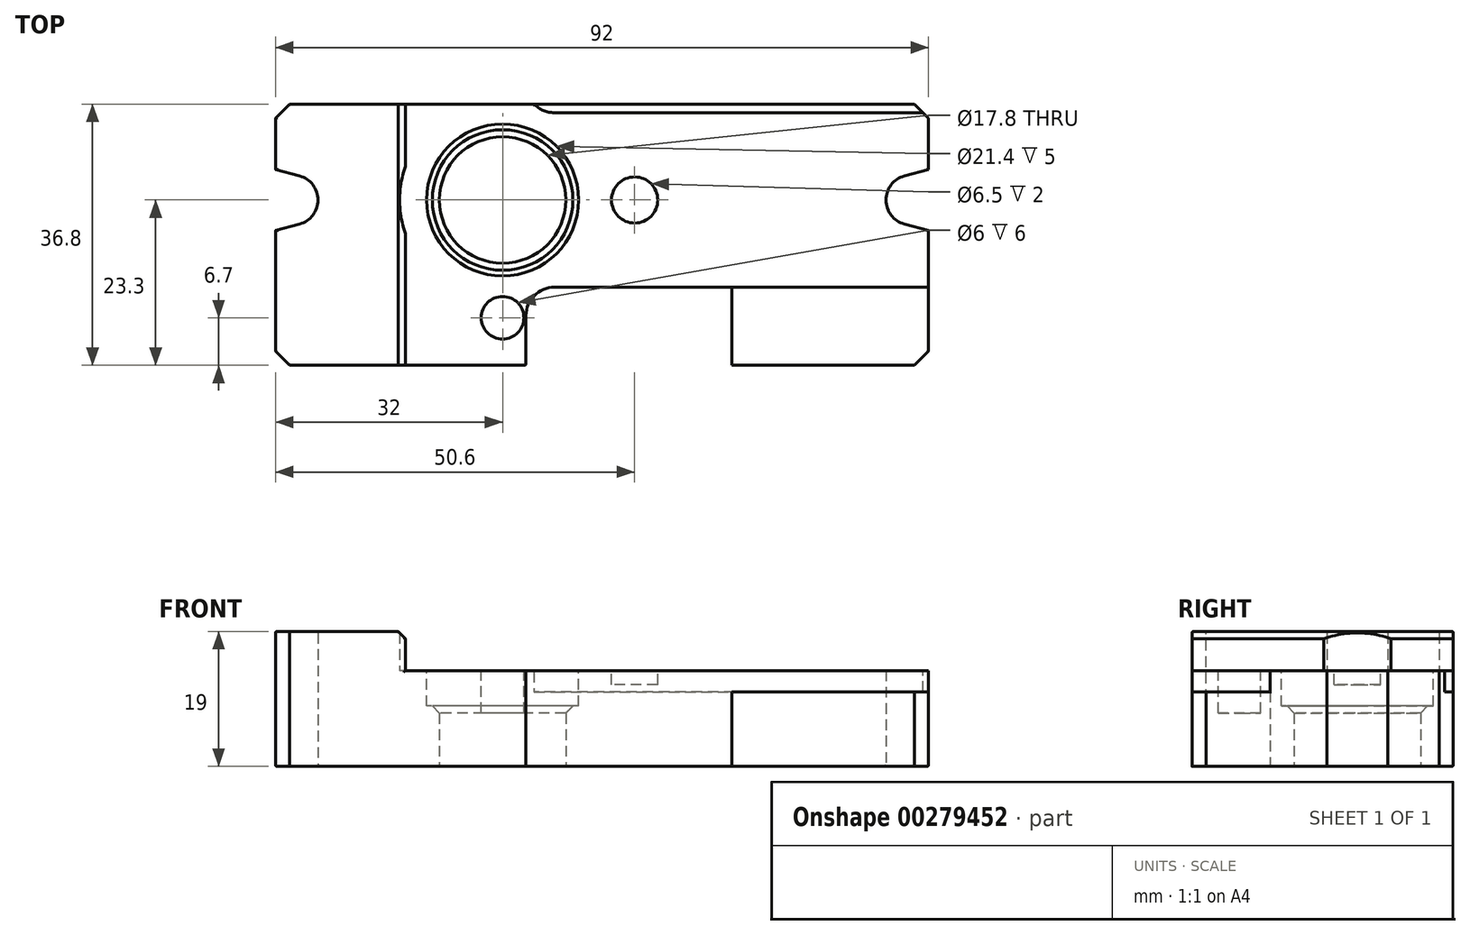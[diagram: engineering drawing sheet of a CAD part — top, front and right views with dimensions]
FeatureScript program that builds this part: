
annotation { "Feature Type Name" : "Feature", "Feature Type Description" : "" }
export const myFeature = defineFeature(function(context is Context, id is Id, definition is map)
    precondition{}
    {
        {
            var Q0;
            Q0=qCreatedBy(makeId("Top.planeOp"),FACE);
            var sketch = newSketch(context, id + "F0", { "sketchPlane" : qUnion([Q0])});
            skLineSegment(sketch, "E0", {"start": v(0, 0) * mm, "end": v(92, 0) * mm});
            skLineSegment(sketch, "E1", {"start": v(92, 0) * mm, "end": v(92, 19) * mm});
            skLineSegment(sketch, "E2", {"start": v(92, 36.8) * mm, "end": v(0, 36.8) * mm});
            skLineSegment(sketch, "E3", {"start": v(0, 36.8) * mm, "end": v(0, 27.6) * mm});
            skLineSegment(sketch, "E4", {"start": v(0, 0) * mm, "end": v(0, 23.3) * mm, "construction": true});
            skLineSegment(sketch, "E5", {"start": v(0, 23.3) * mm, "end": v(2.5, 23.3) * mm, "construction": true});
            skLineSegment(sketch, "E6", {"start": v(2.5, 23.3) * mm, "end": v(32, 23.3) * mm, "construction": true});
            skLineSegment(sketch, "E7", {"start": v(32, 23.3) * mm, "end": v(89.5, 23.3) * mm, "construction": true});
            skArc(sketch, "E8", {"start": v(3.4, 19.92) * mm, "mid": v(6, 23.3) * mm, "end": v(3.4, 26.68) * mm});
            skArc(sketch, "E9", {"start": v(88.6, 26.68) * mm, "mid": v(86, 23.3) * mm, "end": v(88.6, 19.92) * mm});
            skCircle(sketch, "E10", {"center": v(32, 23.3) * mm, "radius": 8.9 * mm});
            skCircle(sketch, "E11", {"center": v(32, 23.3) * mm, "radius": 10.7 * mm, "construction": true});
            skArc(sketch, "E12", {"start": v(18.3, 28.05) * mm, "mid": v(17.5, 23.3) * mm, "end": v(18.3, 18.55) * mm});
            skLineSegment(sketch, "E13", {"start": v(0, 36.8) * mm, "end": v(18.3, 36.8) * mm, "construction": true});
            skLineSegment(sketch, "E14", {"start": v(18.3, 36.8) * mm, "end": v(18.3, 28.05) * mm});
            skLineSegment(sketch, "E15.trimOffspring", {"start": v(18.3, 18.55) * mm, "end": v(18.3, 0) * mm});
            skLineSegment(sketch, "E16", {"start": v(3.4, 26.68) * mm, "end": v(0, 27.6) * mm});
            skLineSegment(sketch, "E17", {"start": v(3.4, 19.92) * mm, "end": v(0, 19) * mm});
            skLineSegment(sketch, "E18.trimOffspring", {"start": v(0, 19) * mm, "end": v(0, 0) * mm});
            skLineSegment(sketch, "E19", {"start": v(88.6, 26.68) * mm, "end": v(92, 27.6) * mm});
            skLineSegment(sketch, "E20", {"start": v(88.6, 19.92) * mm, "end": v(92, 19) * mm});
            skLineSegment(sketch, "E21.trimOffspring", {"start": v(92, 27.6) * mm, "end": v(92, 36.8) * mm});
            skLineSegment(sketch, "E22", {"start": v(0, 0) * mm, "end": v(50.6, 0) * mm, "construction": true});
            skLineSegment(sketch, "E23", {"start": v(50.6, 0) * mm, "end": v(50.6, 23.3) * mm, "construction": true});
            skCircle(sketch, "E24", {"center": v(50.6, 23.3) * mm, "radius": 3.25 * mm, "construction": true});
            skLineSegment(sketch, "E25", {"start": v(0, 0) * mm, "end": v(64.3, 0) * mm, "construction": true});
            skLineSegment(sketch, "E26", {"start": v(64.3, 0) * mm, "end": v(64.3, 36.8) * mm});
            skLineSegment(sketch, "E27", {"start": v(0, 36.8) * mm, "end": v(0, 39.6) * mm, "construction": true});
            skLineSegment(sketch, "E28", {"start": v(0, 39.6) * mm, "end": v(39.3, 39.6) * mm, "construction": true});
            skArc(sketch, "E29", {"start": v(36.44, 36.8) * mm, "mid": v(37.75, 35.91) * mm, "end": v(39.3, 35.6) * mm});
            skLineSegment(sketch, "E30", {"start": v(0, 36.8) * mm, "end": v(0, 35.6) * mm, "construction": true});
            skLineSegment(sketch, "E31", {"start": v(39.3, 35.6) * mm, "end": v(92, 35.6) * mm});
            skArc(sketch, "E32.MirrorC", {"start": v(35.3, 7) * mm, "mid": v(36.47, 9.83) * mm, "end": v(39.3, 11) * mm});
            skLineSegment(sketch, "E33.MirrorCS", {"start": v(39.3, 11) * mm, "end": v(92, 11) * mm});
            skLineSegment(sketch, "E34", {"start": v(35.3, 7) * mm, "end": v(35.3, 0) * mm});
            skLineSegment(sketch, "E35", {"start": v(32, 23.3) * mm, "end": v(32, 6.7) * mm, "construction": true});
            skCircle(sketch, "E36", {"center": v(32, 6.7) * mm, "radius": 3 * mm, "construction": true});
            skSolve(sketch);
        }
        {
            var Q0;
            Q0=qCreatedBy(makeId("Top.planeOp"),FACE);
            cPlane(context, id + "F1", {"entities" : qUnion([Q0]), "cplaneType" : CPlaneType.OFFSET, "offset" : 13.5 * mm, "width" : 150 * mm, "height" : 150 * mm});
        }
        {
            var Q0;
            Q0=qCreatedBy(id+"F1.planeOp",FACE);
            var sketch = newSketch(context, id + "F2", { "sketchPlane" : qUnion([Q0])});
            skCircle(sketch, "E37.0", {"center": v(32, 23.3) * mm, "radius": 10.7 * mm});
            skLineSegment(sketch, "E38.0.0", {"start": v(18.3, 0) * mm, "end": v(18.3, 18.55) * mm});
            skArc(sketch, "E38.0.1", {"start": v(18.3, 18.55) * mm, "mid": v(17.5, 23.3) * mm, "end": v(18.3, 28.05) * mm});
            skLineSegment(sketch, "E38.0.2", {"start": v(18.3, 28.05) * mm, "end": v(18.3, 36.8) * mm});
            skLineSegment(sketch, "E38.0.3", {"start": v(18.3, 36.8) * mm, "end": v(0, 36.8) * mm});
            skLineSegment(sketch, "E38.0.4", {"start": v(0, 36.8) * mm, "end": v(0, 27.6) * mm});
            skLineSegment(sketch, "E38.0.5", {"start": v(0, 27.6) * mm, "end": v(3.4, 26.68) * mm});
            skArc(sketch, "E38.0.6", {"start": v(3.4, 26.68) * mm, "mid": v(6, 23.3) * mm, "end": v(3.4, 19.92) * mm});
            skLineSegment(sketch, "E38.0.7", {"start": v(3.4, 19.92) * mm, "end": v(0, 19) * mm});
            skLineSegment(sketch, "E38.0.8", {"start": v(0, 19) * mm, "end": v(0, 0) * mm});
            skLineSegment(sketch, "E38.0.9", {"start": v(0, 0) * mm, "end": v(18.3, 0) * mm});
            skCircle(sketch, "E39.0", {"center": v(32, 6.7) * mm, "radius": 3 * mm});
            skCircle(sketch, "E40.0", {"center": v(50.6, 23.3) * mm, "radius": 3.25 * mm});
            skLineSegment(sketch, "E41.0.0", {"start": v(35.3, 0) * mm, "end": v(64.3, 0) * mm});
            skLineSegment(sketch, "E41.0.1", {"start": v(64.3, 0) * mm, "end": v(64.3, 11) * mm});
            skLineSegment(sketch, "E41.0.2", {"start": v(64.3, 11) * mm, "end": v(39.3, 11) * mm});
            skArc(sketch, "E41.0.3", {"start": v(39.3, 11) * mm, "mid": v(36.47, 9.83) * mm, "end": v(35.3, 7) * mm});
            skLineSegment(sketch, "E41.0.4", {"start": v(35.3, 7) * mm, "end": v(35.3, 0) * mm});
            skLineSegment(sketch, "E42.0.0", {"start": v(64.3, 11) * mm, "end": v(64.3, 0) * mm});
            skLineSegment(sketch, "E42.0.1", {"start": v(64.3, 0) * mm, "end": v(92, 0) * mm});
            skLineSegment(sketch, "E42.0.2", {"start": v(92, 0) * mm, "end": v(92, 11) * mm});
            skLineSegment(sketch, "E42.0.3", {"start": v(92, 11) * mm, "end": v(64.3, 11) * mm});
            skArc(sketch, "E43.0.0", {"start": v(36.44, 36.8) * mm, "mid": v(37.75, 35.91) * mm, "end": v(39.3, 35.6) * mm});
            skLineSegment(sketch, "E43.0.1", {"start": v(39.3, 35.6) * mm, "end": v(64.3, 35.6) * mm});
            skLineSegment(sketch, "E43.0.2", {"start": v(64.3, 35.6) * mm, "end": v(64.3, 36.8) * mm});
            skLineSegment(sketch, "E43.0.3", {"start": v(64.3, 36.8) * mm, "end": v(36.44, 36.8) * mm});
            skLineSegment(sketch, "E44.0.0", {"start": v(64.3, 36.8) * mm, "end": v(64.3, 35.6) * mm});
            skLineSegment(sketch, "E44.0.1", {"start": v(64.3, 35.6) * mm, "end": v(92, 35.6) * mm});
            skLineSegment(sketch, "E44.0.2", {"start": v(92, 35.6) * mm, "end": v(92, 36.8) * mm});
            skLineSegment(sketch, "E44.0.3", {"start": v(92, 36.8) * mm, "end": v(64.3, 36.8) * mm});
            skLineSegment(sketch, "E45.0.0", {"start": v(92, 35.6) * mm, "end": v(64.3, 35.6) * mm});
            skLineSegment(sketch, "E45.0.1", {"start": v(64.3, 35.6) * mm, "end": v(64.3, 11) * mm});
            skLineSegment(sketch, "E45.0.2", {"start": v(64.3, 11) * mm, "end": v(92, 11) * mm});
            skLineSegment(sketch, "E45.0.3", {"start": v(92, 11) * mm, "end": v(92, 19) * mm});
            skLineSegment(sketch, "E45.0.4", {"start": v(92, 19) * mm, "end": v(88.6, 19.92) * mm});
            skArc(sketch, "E45.0.5", {"start": v(88.6, 19.92) * mm, "mid": v(86, 23.3) * mm, "end": v(88.6, 26.68) * mm});
            skLineSegment(sketch, "E45.0.6", {"start": v(88.6, 26.68) * mm, "end": v(92, 27.6) * mm});
            skLineSegment(sketch, "E45.0.7", {"start": v(92, 27.6) * mm, "end": v(92, 35.6) * mm});
            skSolve(sketch);
        }
        {
            var Q0;
            {var subQ3=sQuery(id+"F0.wireOp",EDGE,"E3");Q0=makeQuery(id+"F0.imprint","IMPRINT",FACE,{"disambiguationData":[TD([[makeQuery(id+"F0.imprint","IMPRINT",EDGE,{"derivedFrom":subQ3}),1.0]])]});}
            var Q1;
            Q1=makeQuery(id+"F0.imprint","IMPRINT",FACE,{"disambiguationData":[TD([[makeQuery(id+"F0.imprint","IMPRINT",EDGE,{"derivedFrom":sQuery(id+"F0.wireOp",EDGE,"E10")}),-1.0]])]});
            var Q2;
            Q2=makeQuery(id+"F0.imprint","IMPRINT",FACE,{"disambiguationData":[TD([[makeQuery(id+"F0.imprint","IMPRINT",EDGE,{"derivedFrom":sQuery(id+"F0.wireOp",EDGE,"E9")}),-1.0]])]});
            extrude(context, id + "F3", {"entities" : qUnion([Q0, Q1, Q2]), "depth" : 13.5 * mm});
        }
        {
            var Q0;
            {var subQ1=sQuery(id+"F0.wireOp",EDGE,"E32.MirrorC");Q0=makeQuery(id+"F0.imprint","IMPRINT",FACE,{"disambiguationData":[TD([[makeQuery(id+"F0.imprint","IMPRINT",EDGE,{"derivedFrom":subQ1}),-1.0]])]});}
            var Q1;
            {var subQ0=sQuery(id+"F0.wireOp",EDGE,"E1");var subQ1=sQuery(id+"F0.wireOp",EDGE,"E0");var subQ2=makeQuery(id+"F0.imprint","INTERSECT",VERTEX,{"derivedFrom":[subQ1,subQ0]});Q1=makeQuery(id+"F0.imprint","IMPRINT",FACE,{"disambiguationData":[TD([[makeQuery(id+"F0.imprint","IMPRINT",EDGE,{"disambiguationData":[TD([[subQ2,1.0]])],"derivedFrom":subQ1}),1.0]])]});}
            var Q2;
            {var subQ0=sQuery(id+"F0.wireOp",EDGE,"E21.trimOffspring");var subQ1=sQuery(id+"F0.wireOp",EDGE,"E2");var subQ2=makeQuery(id+"F0.imprint","INTERSECT",VERTEX,{"derivedFrom":[subQ1,subQ0]});Q2=makeQuery(id+"F0.imprint","IMPRINT",FACE,{"disambiguationData":[TD([[makeQuery(id+"F0.imprint","IMPRINT",EDGE,{"disambiguationData":[TD([[subQ2,-1.0]])],"derivedFrom":subQ1}),1.0]])]});}
            var Q3;
            {var subQ3=sQuery(id+"F0.wireOp",EDGE,"E29");Q3=makeQuery(id+"F0.imprint","IMPRINT",FACE,{"disambiguationData":[TD([[makeQuery(id+"F0.imprint","IMPRINT",EDGE,{"derivedFrom":subQ3}),1.0]])]});}
            extrude(context, id + "F4", {"entities" : qUnion([Q0, Q1, Q2, Q3]), "operationType" : NewBodyOperationType.ADD, "depth" : 10.5 * mm});
        }
        {
            var Q0;
            Q0=makeQuery(id+"F2.imprint","IMPRINT",FACE,{"disambiguationData":[TD([[makeQuery(id+"F2.imprint","IMPRINT",EDGE,{"derivedFrom":sQuery(id+"F2.wireOp",EDGE,"E37.0")}),1.0]])]});
            extrude(context, id + "F5", {"entities" : qUnion([Q0]), "operationType" : NewBodyOperationType.REMOVE, "oppositeDirection" : true, "depth" : 5 * mm});
        }
        {
            var Q0;
            Q0=makeQuery(id+"F2.imprint","IMPRINT",FACE,{"disambiguationData":[TD([[makeQuery(id+"F2.imprint","IMPRINT",EDGE,{"derivedFrom":sQuery(id+"F2.wireOp",EDGE,"E40.0")}),1.0]])]});
            extrude(context, id + "F6", {"entities" : qUnion([Q0]), "operationType" : NewBodyOperationType.REMOVE, "oppositeDirection" : true, "depth" : 2 * mm});
        }
        {
            var Q0;
            Q0=makeQuery(id+"F2.imprint","IMPRINT",FACE,{"disambiguationData":[TD([[makeQuery(id+"F2.imprint","IMPRINT",EDGE,{"derivedFrom":sQuery(id+"F2.wireOp",EDGE,"E39.0")}),1.0]])]});
            extrude(context, id + "F7", {"entities" : qUnion([Q0]), "operationType" : NewBodyOperationType.REMOVE, "oppositeDirection" : true, "depth" : 6 * mm});
        }
        {
            var Q0;
            Q0=makeQuery(id+"F2.imprint","IMPRINT",FACE,{"disambiguationData":[TD([[makeQuery(id+"F2.imprint","IMPRINT",EDGE,{"derivedFrom":sQuery(id+"F2.wireOp",EDGE,"E38.0.0")}),1.0]])]});
            var Q1;
            Q1=makeQuery(id+"F2.imprint","IMPRINT",FACE,{"disambiguationData":[TD([[makeQuery(id+"F2.imprint","IMPRINT",EDGE,{"derivedFrom":sQuery(id+"F2.wireOp",EDGE,"E45.0.0")}),1.0]])]});
            extrude(context, id + "F8", {"entities" : qUnion([Q0, Q1]), "operationType" : NewBodyOperationType.ADD, "depth" : 5.5 * mm});
        }
        {
            var Q0;
            Q0=makeQuery(id+"F8.opExtrude","CAP_EDGE",EDGE,{"disambiguationData":[OSD([sQuery(id+"F2.wireOp",EDGE,"E38.0.0")])],"isStart":false});
            var Q1;
            Q1=makeQuery(id+"F5.boolean.opBoolean","INTERSECT",EDGE,{"derivedFrom":[makeQuery(id+"F3.opExtrude","SWEPT_FACE",FACE,{"disambiguationData":[OSD([sQuery(id+"F0.wireOp",EDGE,"E10")])]}),makeQuery(id+"F5.opExtrude","CAP_FACE",FACE,{"disambiguationData":[OSD([sQuery(id+"F2.wireOp",EDGE,"E37.0")])],"isStart":false})]});
            var Q2;
            Q2=makeQuery(id+"F8.opExtrude","CAP_EDGE",EDGE,{"disambiguationData":[OSD([sQuery(id+"F2.wireOp",EDGE,"E45.0.1")])],"isStart":false});
            chamfer(context, id + "F9", {"entities" : qUnion([Q0, Q1, Q2]), "width" : 1 * mm, "tangentPropagation" : true});
        }
        {
            var Q0;
            Q0=makeQuery(id+"F4.opExtrude","SWEPT_EDGE",EDGE,{"disambiguationData":[OSD([sQuery(id+"F0.wireOp",EDGE,"E0"),sQuery(id+"F0.wireOp",EDGE,"E1")])]});
            var Q1;
            Q1=makeQuery(id+"F8.boolean.opBoolean","MERGE",EDGE,{"derivedFrom":[makeQuery(id+"F3.opExtrude","SWEPT_EDGE",EDGE,{"disambiguationData":[OSD([sQuery(id+"F0.wireOp",EDGE,"E0"),sQuery(id+"F0.wireOp",EDGE,"E18.trimOffspring")])]}),makeQuery(id+"F8.opExtrude","SWEPT_EDGE",EDGE,{"disambiguationData":[OSD([sQuery(id+"F2.wireOp",EDGE,"E38.0.8"),sQuery(id+"F2.wireOp",EDGE,"E38.0.9")])]})]});
            var Q2;
            Q2=makeQuery(id+"F4.opExtrude","SWEPT_EDGE",EDGE,{"disambiguationData":[OSD([sQuery(id+"F0.wireOp",EDGE,"E2"),sQuery(id+"F0.wireOp",EDGE,"E21.trimOffspring")])]});
            var Q3;
            Q3=makeQuery(id+"F8.boolean.opBoolean","MERGE",EDGE,{"derivedFrom":[makeQuery(id+"F3.opExtrude","SWEPT_EDGE",EDGE,{"disambiguationData":[OSD([sQuery(id+"F0.wireOp",EDGE,"E2"),sQuery(id+"F0.wireOp",EDGE,"E3")])]}),makeQuery(id+"F8.opExtrude","SWEPT_EDGE",EDGE,{"disambiguationData":[OSD([sQuery(id+"F2.wireOp",EDGE,"E38.0.3"),sQuery(id+"F2.wireOp",EDGE,"E38.0.4")])]})]});
            chamfer(context, id + "F10", {"entities" : qUnion([Q0, Q1, Q2, Q3]), "width" : 2 * mm, "tangentPropagation" : true});
        }
        {
            var Q0;
            Q0=makeQuery(id+"F6.boolean.opBoolean","COPY",EDGE,{"derivedFrom":makeQuery(id+"F6.opExtrude","CAP_EDGE",EDGE,{"disambiguationData":[OSD([sQuery(id+"F2.wireOp",EDGE,"E40.0")])],"isStart":true})});
            var Q1;
            Q1=makeQuery(id+"F3.opExtrude","CAP_EDGE",EDGE,{"disambiguationData":[OSD([sQuery(id+"F0.wireOp",EDGE,"E34")])],"isStart":false});
            var Q2;
            Q2=makeQuery(id+"F8.opExtrude","SWEPT_EDGE",EDGE,{"disambiguationData":[OSD([sQuery(id+"F2.wireOp",EDGE,"E41.0.2"),sQuery(id+"F2.wireOp",EDGE,"E42.0.0"),sQuery(id+"F2.wireOp",EDGE,"E45.0.1"),sQuery(id+"F2.wireOp",EDGE,"E45.0.2")])]});
            var Q3;
            Q3=makeQuery(id+"F9.opChamfer","BLEND_EDGE",EDGE,{"blendedFrom":[makeQuery(id+"F8.opExtrude","CAP_EDGE",EDGE,{"disambiguationData":[OSD([sQuery(id+"F2.wireOp",EDGE,"E45.0.1")])],"isStart":false}),makeQuery(id+"F8.boolean.opBoolean","MERGE",FACE,{"derivedFrom":[makeQuery(id+"F3.opExtrude","SWEPT_FACE",FACE,{"disambiguationData":[OSD([sQuery(id+"F0.wireOp",EDGE,"E33.MirrorCS")])]}),makeQuery(id+"F8.opExtrude","SWEPT_FACE",FACE,{"disambiguationData":[OSD([sQuery(id+"F2.wireOp",EDGE,"E45.0.2")])]})]})],"blendedInto":[makeQuery(id+"F8.boolean.opBoolean","MERGE",FACE,{"derivedFrom":[makeQuery(id+"F3.opExtrude","SWEPT_FACE",FACE,{"disambiguationData":[OSD([sQuery(id+"F0.wireOp",EDGE,"E33.MirrorCS")])]}),makeQuery(id+"F8.opExtrude","SWEPT_FACE",FACE,{"disambiguationData":[OSD([sQuery(id+"F2.wireOp",EDGE,"E45.0.2")])]})]})]});
            var Q4;
            Q4=makeQuery(id+"F8.opExtrude","CAP_EDGE",EDGE,{"disambiguationData":[OSD([sQuery(id+"F2.wireOp",EDGE,"E45.0.2")])],"isStart":false});
            var Q5;
            Q5=makeQuery(id+"F8.boolean.opBoolean","MERGE",EDGE,{"derivedFrom":[makeQuery(id+"F3.opExtrude","SWEPT_EDGE",EDGE,{"disambiguationData":[OSD([sQuery(id+"F0.wireOp",EDGE,"E1"),sQuery(id+"F0.wireOp",EDGE,"E33.MirrorCS")])]}),makeQuery(id+"F8.opExtrude","SWEPT_EDGE",EDGE,{"disambiguationData":[OSD([sQuery(id+"F2.wireOp",EDGE,"E42.0.2"),sQuery(id+"F2.wireOp",EDGE,"E45.0.2"),sQuery(id+"F2.wireOp",EDGE,"E45.0.3")])]})]});
            var Q6;
            Q6=makeQuery(id+"F4.opExtrude","CAP_EDGE",EDGE,{"disambiguationData":[OSD([sQuery(id+"F0.wireOp",EDGE,"E1")])],"isStart":false});
            var Q7;
            {var subQ0=sQuery(id+"F0.wireOp",EDGE,"E1");var subQ1=sQuery(id+"F0.wireOp",EDGE,"E0");Q7=makeQuery(id+"F10.opChamfer","BLEND_EDGE",EDGE,{"blendedFrom":[makeQuery(id+"F4.opExtrude","SWEPT_EDGE",EDGE,{"disambiguationData":[OSD([subQ1,subQ0])]}),makeQuery(id+"F4.opExtrude","CAP_FACE",FACE,{"disambiguationData":[OSD([subQ1,subQ0,sQuery(id+"F0.wireOp",EDGE,"E32.MirrorC"),sQuery(id+"F0.wireOp",EDGE,"E33.MirrorCS"),sQuery(id+"F0.wireOp",EDGE,"E34")])],"isStart":false})],"blendedInto":[makeQuery(id+"F4.opExtrude","CAP_FACE",FACE,{"disambiguationData":[OSD([subQ1,subQ0,sQuery(id+"F0.wireOp",EDGE,"E32.MirrorC"),sQuery(id+"F0.wireOp",EDGE,"E33.MirrorCS"),sQuery(id+"F0.wireOp",EDGE,"E34")])],"isStart":false})]});}
            var Q8;
            Q8=makeQuery(id+"F4.opExtrude","CAP_EDGE",EDGE,{"disambiguationData":[OSD([sQuery(id+"F0.wireOp",EDGE,"E0")])],"isStart":false});
            var Q9;
            Q9=makeQuery(id+"F3.opExtrude","SWEPT_EDGE",EDGE,{"disambiguationData":[OSD([sQuery(id+"F0.wireOp",EDGE,"E0"),sQuery(id+"F0.wireOp",EDGE,"E34")])]});
            var Q10;
            Q10=makeQuery(id+"F3.opExtrude","CAP_EDGE",EDGE,{"disambiguationData":[OSD([sQuery(id+"F0.wireOp",EDGE,"E0")])],"isStart":false});
            var Q11;
            Q11=makeQuery(id+"F8.opExtrude","SWEPT_EDGE",EDGE,{"disambiguationData":[OSD([sQuery(id+"F2.wireOp",EDGE,"E38.0.0"),sQuery(id+"F2.wireOp",EDGE,"E38.0.9")])]});
            var Q12;
            {var subQ0=sQuery(id+"F0.wireOp",EDGE,"E0");Q12=makeQuery(id+"F9.opChamfer","BLEND_EDGE",EDGE,{"blendedFrom":[makeQuery(id+"F8.opExtrude","CAP_EDGE",EDGE,{"disambiguationData":[OSD([sQuery(id+"F2.wireOp",EDGE,"E38.0.0")])],"isStart":false}),makeQuery(id+"F8.boolean.opBoolean","MERGE",FACE,{"derivedFrom":[makeQuery(id+"F4.boolean.opBoolean","MERGE",FACE,{"derivedFrom":[makeQuery(id+"F3.opExtrude","SWEPT_FACE",FACE,{"disambiguationData":[OSD([subQ0])]}),makeQuery(id+"F4.opExtrude","SWEPT_FACE",FACE,{"disambiguationData":[OSD([subQ0])]})]}),makeQuery(id+"F8.opExtrude","SWEPT_FACE",FACE,{"disambiguationData":[OSD([sQuery(id+"F2.wireOp",EDGE,"E38.0.9")])]})]})],"blendedInto":[makeQuery(id+"F8.boolean.opBoolean","MERGE",FACE,{"derivedFrom":[makeQuery(id+"F4.boolean.opBoolean","MERGE",FACE,{"derivedFrom":[makeQuery(id+"F3.opExtrude","SWEPT_FACE",FACE,{"disambiguationData":[OSD([subQ0])]}),makeQuery(id+"F4.opExtrude","SWEPT_FACE",FACE,{"disambiguationData":[OSD([subQ0])]})]}),makeQuery(id+"F8.opExtrude","SWEPT_FACE",FACE,{"disambiguationData":[OSD([sQuery(id+"F2.wireOp",EDGE,"E38.0.9")])]})]})]});}
            var Q13;
            Q13=makeQuery(id+"F8.opExtrude","CAP_EDGE",EDGE,{"disambiguationData":[OSD([sQuery(id+"F2.wireOp",EDGE,"E38.0.9")])],"isStart":false});
            var Q14;
            {var subQ0=sQuery(id+"F2.wireOp",EDGE,"E38.0.9");var subQ1=sQuery(id+"F2.wireOp",EDGE,"E38.0.8");Q14=makeQuery(id+"F10.opChamfer","BLEND_EDGE",EDGE,{"blendedFrom":[makeQuery(id+"F8.boolean.opBoolean","MERGE",EDGE,{"derivedFrom":[makeQuery(id+"F3.opExtrude","SWEPT_EDGE",EDGE,{"disambiguationData":[OSD([sQuery(id+"F0.wireOp",EDGE,"E0"),sQuery(id+"F0.wireOp",EDGE,"E18.trimOffspring")])]}),makeQuery(id+"F8.opExtrude","SWEPT_EDGE",EDGE,{"disambiguationData":[OSD([subQ1,subQ0])]})]}),makeQuery(id+"F8.opExtrude","CAP_FACE",FACE,{"disambiguationData":[OSD([sQuery(id+"F2.wireOp",EDGE,"E38.0.0"),sQuery(id+"F2.wireOp",EDGE,"E38.0.1"),sQuery(id+"F2.wireOp",EDGE,"E38.0.2"),sQuery(id+"F2.wireOp",EDGE,"E38.0.3"),sQuery(id+"F2.wireOp",EDGE,"E38.0.4"),sQuery(id+"F2.wireOp",EDGE,"E38.0.5"),sQuery(id+"F2.wireOp",EDGE,"E38.0.6"),sQuery(id+"F2.wireOp",EDGE,"E38.0.7"),subQ1,subQ0])],"isStart":false})],"blendedInto":[makeQuery(id+"F8.opExtrude","CAP_FACE",FACE,{"disambiguationData":[OSD([sQuery(id+"F2.wireOp",EDGE,"E38.0.0"),sQuery(id+"F2.wireOp",EDGE,"E38.0.1"),sQuery(id+"F2.wireOp",EDGE,"E38.0.2"),sQuery(id+"F2.wireOp",EDGE,"E38.0.3"),sQuery(id+"F2.wireOp",EDGE,"E38.0.4"),sQuery(id+"F2.wireOp",EDGE,"E38.0.5"),sQuery(id+"F2.wireOp",EDGE,"E38.0.6"),sQuery(id+"F2.wireOp",EDGE,"E38.0.7"),subQ1,subQ0])],"isStart":false})]});}
            var Q15;
            Q15=makeQuery(id+"F8.opExtrude","CAP_EDGE",EDGE,{"disambiguationData":[OSD([sQuery(id+"F2.wireOp",EDGE,"E38.0.8")])],"isStart":false});
            var Q16;
            Q16=makeQuery(id+"F8.opExtrude","CAP_EDGE",EDGE,{"disambiguationData":[OSD([sQuery(id+"F2.wireOp",EDGE,"E38.0.7")])],"isStart":false});
            var Q17;
            Q17=makeQuery(id+"F8.opExtrude","CAP_EDGE",EDGE,{"disambiguationData":[OSD([sQuery(id+"F2.wireOp",EDGE,"E38.0.6")])],"isStart":false});
            var Q18;
            Q18=makeQuery(id+"F8.opExtrude","CAP_EDGE",EDGE,{"disambiguationData":[OSD([sQuery(id+"F2.wireOp",EDGE,"E38.0.4")])],"isStart":false});
            var Q19;
            {var subQ0=sQuery(id+"F2.wireOp",EDGE,"E38.0.4");var subQ1=sQuery(id+"F2.wireOp",EDGE,"E38.0.3");Q19=makeQuery(id+"F10.opChamfer","BLEND_EDGE",EDGE,{"blendedFrom":[makeQuery(id+"F8.boolean.opBoolean","MERGE",EDGE,{"derivedFrom":[makeQuery(id+"F3.opExtrude","SWEPT_EDGE",EDGE,{"disambiguationData":[OSD([sQuery(id+"F0.wireOp",EDGE,"E2"),sQuery(id+"F0.wireOp",EDGE,"E3")])]}),makeQuery(id+"F8.opExtrude","SWEPT_EDGE",EDGE,{"disambiguationData":[OSD([subQ1,subQ0])]})]}),makeQuery(id+"F8.opExtrude","CAP_FACE",FACE,{"disambiguationData":[OSD([sQuery(id+"F2.wireOp",EDGE,"E38.0.0"),sQuery(id+"F2.wireOp",EDGE,"E38.0.1"),sQuery(id+"F2.wireOp",EDGE,"E38.0.2"),subQ1,subQ0,sQuery(id+"F2.wireOp",EDGE,"E38.0.5"),sQuery(id+"F2.wireOp",EDGE,"E38.0.6"),sQuery(id+"F2.wireOp",EDGE,"E38.0.7"),sQuery(id+"F2.wireOp",EDGE,"E38.0.8"),sQuery(id+"F2.wireOp",EDGE,"E38.0.9")])],"isStart":false})],"blendedInto":[makeQuery(id+"F8.opExtrude","CAP_FACE",FACE,{"disambiguationData":[OSD([sQuery(id+"F2.wireOp",EDGE,"E38.0.0"),sQuery(id+"F2.wireOp",EDGE,"E38.0.1"),sQuery(id+"F2.wireOp",EDGE,"E38.0.2"),subQ1,subQ0,sQuery(id+"F2.wireOp",EDGE,"E38.0.5"),sQuery(id+"F2.wireOp",EDGE,"E38.0.6"),sQuery(id+"F2.wireOp",EDGE,"E38.0.7"),sQuery(id+"F2.wireOp",EDGE,"E38.0.8"),sQuery(id+"F2.wireOp",EDGE,"E38.0.9")])],"isStart":false})]});}
            var Q20;
            Q20=makeQuery(id+"F8.opExtrude","CAP_EDGE",EDGE,{"disambiguationData":[OSD([sQuery(id+"F2.wireOp",EDGE,"E38.0.3")])],"isStart":false});
            var Q21;
            {var subQ0=sQuery(id+"F0.wireOp",EDGE,"E2");Q21=makeQuery(id+"F9.opChamfer","BLEND_EDGE",EDGE,{"blendedFrom":[makeQuery(id+"F8.opExtrude","CAP_EDGE",EDGE,{"disambiguationData":[OSD([sQuery(id+"F2.wireOp",EDGE,"E38.0.0")])],"isStart":false}),makeQuery(id+"F8.boolean.opBoolean","MERGE",FACE,{"derivedFrom":[makeQuery(id+"F4.boolean.opBoolean","MERGE",FACE,{"derivedFrom":[makeQuery(id+"F3.opExtrude","SWEPT_FACE",FACE,{"disambiguationData":[OSD([subQ0])]}),makeQuery(id+"F4.opExtrude","SWEPT_FACE",FACE,{"disambiguationData":[OSD([subQ0])]})]}),makeQuery(id+"F8.opExtrude","SWEPT_FACE",FACE,{"disambiguationData":[OSD([sQuery(id+"F2.wireOp",EDGE,"E38.0.3")])]})]})],"blendedInto":[makeQuery(id+"F8.boolean.opBoolean","MERGE",FACE,{"derivedFrom":[makeQuery(id+"F4.boolean.opBoolean","MERGE",FACE,{"derivedFrom":[makeQuery(id+"F3.opExtrude","SWEPT_FACE",FACE,{"disambiguationData":[OSD([subQ0])]}),makeQuery(id+"F4.opExtrude","SWEPT_FACE",FACE,{"disambiguationData":[OSD([subQ0])]})]}),makeQuery(id+"F8.opExtrude","SWEPT_FACE",FACE,{"disambiguationData":[OSD([sQuery(id+"F2.wireOp",EDGE,"E38.0.3")])]})]})]});}
            var Q22;
            Q22=makeQuery(id+"F8.opExtrude","SWEPT_EDGE",EDGE,{"disambiguationData":[OSD([sQuery(id+"F2.wireOp",EDGE,"E38.0.2"),sQuery(id+"F2.wireOp",EDGE,"E38.0.3")])]});
            var Q23;
            Q23=makeQuery(id+"F3.opExtrude","CAP_EDGE",EDGE,{"disambiguationData":[OSD([sQuery(id+"F0.wireOp",EDGE,"E2")])],"isStart":false});
            var Q24;
            Q24=makeQuery(id+"F8.opExtrude","CAP_EDGE",EDGE,{"disambiguationData":[OSD([sQuery(id+"F2.wireOp",EDGE,"E45.0.3")])],"isStart":false});
            var Q25;
            Q25=makeQuery(id+"F8.opExtrude","CAP_EDGE",EDGE,{"disambiguationData":[OSD([sQuery(id+"F2.wireOp",EDGE,"E45.0.4")])],"isStart":false});
            var Q26;
            Q26=makeQuery(id+"F8.opExtrude","CAP_EDGE",EDGE,{"disambiguationData":[OSD([sQuery(id+"F2.wireOp",EDGE,"E45.0.5")])],"isStart":false});
            var Q27;
            Q27=makeQuery(id+"F8.opExtrude","CAP_EDGE",EDGE,{"disambiguationData":[OSD([sQuery(id+"F2.wireOp",EDGE,"E45.0.6")])],"isStart":false});
            var Q28;
            Q28=makeQuery(id+"F8.opExtrude","CAP_EDGE",EDGE,{"disambiguationData":[OSD([sQuery(id+"F2.wireOp",EDGE,"E45.0.7")])],"isStart":false});
            var Q29;
            Q29=makeQuery(id+"F10.opChamfer","BLEND_EDGE",EDGE,{"blendedFrom":[makeQuery(id+"F4.opExtrude","SWEPT_EDGE",EDGE,{"disambiguationData":[OSD([sQuery(id+"F0.wireOp",EDGE,"E2"),sQuery(id+"F0.wireOp",EDGE,"E21.trimOffspring")])]}),makeQuery(id+"F8.opExtrude","CAP_FACE",FACE,{"disambiguationData":[OSD([sQuery(id+"F2.wireOp",EDGE,"E45.0.0"),sQuery(id+"F2.wireOp",EDGE,"E45.0.1"),sQuery(id+"F2.wireOp",EDGE,"E45.0.2"),sQuery(id+"F2.wireOp",EDGE,"E45.0.3"),sQuery(id+"F2.wireOp",EDGE,"E45.0.4"),sQuery(id+"F2.wireOp",EDGE,"E45.0.5"),sQuery(id+"F2.wireOp",EDGE,"E45.0.6"),sQuery(id+"F2.wireOp",EDGE,"E45.0.7")])],"isStart":false})],"blendedInto":[makeQuery(id+"F8.opExtrude","CAP_FACE",FACE,{"disambiguationData":[OSD([sQuery(id+"F2.wireOp",EDGE,"E45.0.0"),sQuery(id+"F2.wireOp",EDGE,"E45.0.1"),sQuery(id+"F2.wireOp",EDGE,"E45.0.2"),sQuery(id+"F2.wireOp",EDGE,"E45.0.3"),sQuery(id+"F2.wireOp",EDGE,"E45.0.4"),sQuery(id+"F2.wireOp",EDGE,"E45.0.5"),sQuery(id+"F2.wireOp",EDGE,"E45.0.6"),sQuery(id+"F2.wireOp",EDGE,"E45.0.7")])],"isStart":false})]});
            var Q30;
            Q30=makeQuery(id+"F8.opExtrude","CAP_EDGE",EDGE,{"disambiguationData":[OSD([sQuery(id+"F2.wireOp",EDGE,"E45.0.0")])],"isStart":false});
            var Q31;
            Q31=makeQuery(id+"F9.opChamfer","BLEND_EDGE",EDGE,{"blendedFrom":[makeQuery(id+"F8.opExtrude","CAP_EDGE",EDGE,{"disambiguationData":[OSD([sQuery(id+"F2.wireOp",EDGE,"E45.0.1")])],"isStart":false}),makeQuery(id+"F8.boolean.opBoolean","MERGE",FACE,{"derivedFrom":[makeQuery(id+"F3.opExtrude","SWEPT_FACE",FACE,{"disambiguationData":[OSD([sQuery(id+"F0.wireOp",EDGE,"E31")])]}),makeQuery(id+"F8.opExtrude","SWEPT_FACE",FACE,{"disambiguationData":[OSD([sQuery(id+"F2.wireOp",EDGE,"E45.0.0")])]})]})],"blendedInto":[makeQuery(id+"F8.boolean.opBoolean","MERGE",FACE,{"derivedFrom":[makeQuery(id+"F3.opExtrude","SWEPT_FACE",FACE,{"disambiguationData":[OSD([sQuery(id+"F0.wireOp",EDGE,"E31")])]}),makeQuery(id+"F8.opExtrude","SWEPT_FACE",FACE,{"disambiguationData":[OSD([sQuery(id+"F2.wireOp",EDGE,"E45.0.0")])]})]})]});
            var Q32;
            Q32=makeQuery(id+"F8.opExtrude","SWEPT_EDGE",EDGE,{"disambiguationData":[OSD([sQuery(id+"F2.wireOp",EDGE,"E43.0.1"),sQuery(id+"F2.wireOp",EDGE,"E44.0.0"),sQuery(id+"F2.wireOp",EDGE,"E45.0.0"),sQuery(id+"F2.wireOp",EDGE,"E45.0.1")])]});
            var Q33;
            Q33=makeQuery(id+"F3.opExtrude","CAP_EDGE",EDGE,{"disambiguationData":[OSD([sQuery(id+"F0.wireOp",EDGE,"E31")])],"isStart":false});
            var Q34;
            Q34=makeQuery(id+"F3.opExtrude","CAP_EDGE",EDGE,{"disambiguationData":[OSD([sQuery(id+"F0.wireOp",EDGE,"E29")])],"isStart":false});
            var Q35;
            {var subQ0=sQuery(id+"F0.wireOp",EDGE,"E31");var subQ1=sQuery(id+"F0.wireOp",EDGE,"E29");var subQ2=sQuery(id+"F0.wireOp",EDGE,"E21.trimOffspring");var subQ3=sQuery(id+"F0.wireOp",EDGE,"E2");var subQ4=sQuery(id+"F0.wireOp",EDGE,"E34");var subQ5=sQuery(id+"F0.wireOp",EDGE,"E33.MirrorCS");var subQ6=sQuery(id+"F0.wireOp",EDGE,"E32.MirrorC");var subQ7=sQuery(id+"F0.wireOp",EDGE,"E1");var subQ8=sQuery(id+"F0.wireOp",EDGE,"E0");var subQ9=sQuery(id+"F0.wireOp",EDGE,"E18.trimOffspring");Q35=makeQuery(id+"F10.opChamfer","BLEND_EDGE",EDGE,{"blendedFrom":[makeQuery(id+"F8.boolean.opBoolean","MERGE",EDGE,{"derivedFrom":[makeQuery(id+"F3.opExtrude","SWEPT_EDGE",EDGE,{"disambiguationData":[OSD([subQ8,subQ9])]}),makeQuery(id+"F8.opExtrude","SWEPT_EDGE",EDGE,{"disambiguationData":[OSD([sQuery(id+"F2.wireOp",EDGE,"E38.0.8"),sQuery(id+"F2.wireOp",EDGE,"E38.0.9")])]})]}),makeQuery(id+"F4.boolean.opBoolean","MERGE",FACE,{"derivedFrom":[makeQuery(id+"F3.opExtrude","CAP_FACE",FACE,{"disambiguationData":[OSD([subQ8,subQ7,subQ3,sQuery(id+"F0.wireOp",EDGE,"E3"),sQuery(id+"F0.wireOp",EDGE,"E8"),sQuery(id+"F0.wireOp",EDGE,"E9"),sQuery(id+"F0.wireOp",EDGE,"E10"),sQuery(id+"F0.wireOp",EDGE,"E16"),sQuery(id+"F0.wireOp",EDGE,"E17"),subQ9,sQuery(id+"F0.wireOp",EDGE,"E19"),sQuery(id+"F0.wireOp",EDGE,"E20"),subQ2,subQ1,subQ0,subQ6,subQ5,subQ4])],"isStart":true}),makeQuery(id+"F4.opExtrude","CAP_FACE",FACE,{"disambiguationData":[OSD([subQ8,subQ7,subQ6,subQ5,subQ4])],"isStart":true}),makeQuery(id+"F4.opExtrude","CAP_FACE",FACE,{"disambiguationData":[OSD([subQ3,subQ2,subQ1,subQ0])],"isStart":true})]})],"blendedInto":[makeQuery(id+"F4.boolean.opBoolean","MERGE",FACE,{"derivedFrom":[makeQuery(id+"F3.opExtrude","CAP_FACE",FACE,{"disambiguationData":[OSD([subQ8,subQ7,subQ3,sQuery(id+"F0.wireOp",EDGE,"E3"),sQuery(id+"F0.wireOp",EDGE,"E8"),sQuery(id+"F0.wireOp",EDGE,"E9"),sQuery(id+"F0.wireOp",EDGE,"E10"),sQuery(id+"F0.wireOp",EDGE,"E16"),sQuery(id+"F0.wireOp",EDGE,"E17"),subQ9,sQuery(id+"F0.wireOp",EDGE,"E19"),sQuery(id+"F0.wireOp",EDGE,"E20"),subQ2,subQ1,subQ0,subQ6,subQ5,subQ4])],"isStart":true}),makeQuery(id+"F4.opExtrude","CAP_FACE",FACE,{"disambiguationData":[OSD([subQ8,subQ7,subQ6,subQ5,subQ4])],"isStart":true}),makeQuery(id+"F4.opExtrude","CAP_FACE",FACE,{"disambiguationData":[OSD([subQ3,subQ2,subQ1,subQ0])],"isStart":true})]})]});}
            var Q36;
            {var subQ0=sQuery(id+"F0.wireOp",EDGE,"E0");Q36=makeQuery(id+"F4.boolean.opBoolean","MERGE",EDGE,{"derivedFrom":[makeQuery(id+"F3.opExtrude","CAP_EDGE",EDGE,{"disambiguationData":[OSD([subQ0])],"isStart":true}),makeQuery(id+"F4.opExtrude","CAP_EDGE",EDGE,{"disambiguationData":[OSD([subQ0])],"isStart":true})]});}
            var Q37;
            {var subQ0=sQuery(id+"F0.wireOp",EDGE,"E31");var subQ1=sQuery(id+"F0.wireOp",EDGE,"E29");var subQ2=sQuery(id+"F0.wireOp",EDGE,"E21.trimOffspring");var subQ3=sQuery(id+"F0.wireOp",EDGE,"E2");var subQ4=sQuery(id+"F0.wireOp",EDGE,"E34");var subQ5=sQuery(id+"F0.wireOp",EDGE,"E33.MirrorCS");var subQ6=sQuery(id+"F0.wireOp",EDGE,"E32.MirrorC");var subQ7=sQuery(id+"F0.wireOp",EDGE,"E1");var subQ8=sQuery(id+"F0.wireOp",EDGE,"E0");Q37=makeQuery(id+"F10.opChamfer","BLEND_EDGE",EDGE,{"blendedFrom":[makeQuery(id+"F4.opExtrude","SWEPT_EDGE",EDGE,{"disambiguationData":[OSD([subQ8,subQ7])]}),makeQuery(id+"F4.boolean.opBoolean","MERGE",FACE,{"derivedFrom":[makeQuery(id+"F3.opExtrude","CAP_FACE",FACE,{"disambiguationData":[OSD([subQ8,subQ7,subQ3,sQuery(id+"F0.wireOp",EDGE,"E3"),sQuery(id+"F0.wireOp",EDGE,"E8"),sQuery(id+"F0.wireOp",EDGE,"E9"),sQuery(id+"F0.wireOp",EDGE,"E10"),sQuery(id+"F0.wireOp",EDGE,"E16"),sQuery(id+"F0.wireOp",EDGE,"E17"),sQuery(id+"F0.wireOp",EDGE,"E18.trimOffspring"),sQuery(id+"F0.wireOp",EDGE,"E19"),sQuery(id+"F0.wireOp",EDGE,"E20"),subQ2,subQ1,subQ0,subQ6,subQ5,subQ4])],"isStart":true}),makeQuery(id+"F4.opExtrude","CAP_FACE",FACE,{"disambiguationData":[OSD([subQ8,subQ7,subQ6,subQ5,subQ4])],"isStart":true}),makeQuery(id+"F4.opExtrude","CAP_FACE",FACE,{"disambiguationData":[OSD([subQ3,subQ2,subQ1,subQ0])],"isStart":true})]})],"blendedInto":[makeQuery(id+"F4.boolean.opBoolean","MERGE",FACE,{"derivedFrom":[makeQuery(id+"F3.opExtrude","CAP_FACE",FACE,{"disambiguationData":[OSD([subQ8,subQ7,subQ3,sQuery(id+"F0.wireOp",EDGE,"E3"),sQuery(id+"F0.wireOp",EDGE,"E8"),sQuery(id+"F0.wireOp",EDGE,"E9"),sQuery(id+"F0.wireOp",EDGE,"E10"),sQuery(id+"F0.wireOp",EDGE,"E16"),sQuery(id+"F0.wireOp",EDGE,"E17"),sQuery(id+"F0.wireOp",EDGE,"E18.trimOffspring"),sQuery(id+"F0.wireOp",EDGE,"E19"),sQuery(id+"F0.wireOp",EDGE,"E20"),subQ2,subQ1,subQ0,subQ6,subQ5,subQ4])],"isStart":true}),makeQuery(id+"F4.opExtrude","CAP_FACE",FACE,{"disambiguationData":[OSD([subQ8,subQ7,subQ6,subQ5,subQ4])],"isStart":true}),makeQuery(id+"F4.opExtrude","CAP_FACE",FACE,{"disambiguationData":[OSD([subQ3,subQ2,subQ1,subQ0])],"isStart":true})]})]});}
            var Q38;
            {var subQ0=sQuery(id+"F0.wireOp",EDGE,"E1");Q38=makeQuery(id+"F4.boolean.opBoolean","MERGE",EDGE,{"derivedFrom":[makeQuery(id+"F3.opExtrude","CAP_EDGE",EDGE,{"disambiguationData":[OSD([subQ0])],"isStart":true}),makeQuery(id+"F4.opExtrude","CAP_EDGE",EDGE,{"disambiguationData":[OSD([subQ0])],"isStart":true})]});}
            var Q39;
            Q39=makeQuery(id+"F3.opExtrude","CAP_EDGE",EDGE,{"disambiguationData":[OSD([sQuery(id+"F0.wireOp",EDGE,"E20")])],"isStart":true});
            var Q40;
            Q40=makeQuery(id+"F3.opExtrude","CAP_EDGE",EDGE,{"disambiguationData":[OSD([sQuery(id+"F0.wireOp",EDGE,"E9")])],"isStart":true});
            var Q41;
            {var subQ0=sQuery(id+"F0.wireOp",EDGE,"E21.trimOffspring");Q41=makeQuery(id+"F4.boolean.opBoolean","MERGE",EDGE,{"derivedFrom":[makeQuery(id+"F3.opExtrude","CAP_EDGE",EDGE,{"disambiguationData":[OSD([subQ0])],"isStart":true}),makeQuery(id+"F4.opExtrude","CAP_EDGE",EDGE,{"disambiguationData":[OSD([subQ0])],"isStart":true})]});}
            var Q42;
            {var subQ0=sQuery(id+"F0.wireOp",EDGE,"E31");var subQ1=sQuery(id+"F0.wireOp",EDGE,"E29");var subQ2=sQuery(id+"F0.wireOp",EDGE,"E21.trimOffspring");var subQ3=sQuery(id+"F0.wireOp",EDGE,"E2");var subQ4=sQuery(id+"F0.wireOp",EDGE,"E34");var subQ5=sQuery(id+"F0.wireOp",EDGE,"E33.MirrorCS");var subQ6=sQuery(id+"F0.wireOp",EDGE,"E32.MirrorC");var subQ7=sQuery(id+"F0.wireOp",EDGE,"E1");var subQ8=sQuery(id+"F0.wireOp",EDGE,"E0");Q42=makeQuery(id+"F10.opChamfer","BLEND_EDGE",EDGE,{"blendedFrom":[makeQuery(id+"F4.opExtrude","SWEPT_EDGE",EDGE,{"disambiguationData":[OSD([subQ3,subQ2])]}),makeQuery(id+"F4.boolean.opBoolean","MERGE",FACE,{"derivedFrom":[makeQuery(id+"F3.opExtrude","CAP_FACE",FACE,{"disambiguationData":[OSD([subQ8,subQ7,subQ3,sQuery(id+"F0.wireOp",EDGE,"E3"),sQuery(id+"F0.wireOp",EDGE,"E8"),sQuery(id+"F0.wireOp",EDGE,"E9"),sQuery(id+"F0.wireOp",EDGE,"E10"),sQuery(id+"F0.wireOp",EDGE,"E16"),sQuery(id+"F0.wireOp",EDGE,"E17"),sQuery(id+"F0.wireOp",EDGE,"E18.trimOffspring"),sQuery(id+"F0.wireOp",EDGE,"E19"),sQuery(id+"F0.wireOp",EDGE,"E20"),subQ2,subQ1,subQ0,subQ6,subQ5,subQ4])],"isStart":true}),makeQuery(id+"F4.opExtrude","CAP_FACE",FACE,{"disambiguationData":[OSD([subQ8,subQ7,subQ6,subQ5,subQ4])],"isStart":true}),makeQuery(id+"F4.opExtrude","CAP_FACE",FACE,{"disambiguationData":[OSD([subQ3,subQ2,subQ1,subQ0])],"isStart":true})]})],"blendedInto":[makeQuery(id+"F4.boolean.opBoolean","MERGE",FACE,{"derivedFrom":[makeQuery(id+"F3.opExtrude","CAP_FACE",FACE,{"disambiguationData":[OSD([subQ8,subQ7,subQ3,sQuery(id+"F0.wireOp",EDGE,"E3"),sQuery(id+"F0.wireOp",EDGE,"E8"),sQuery(id+"F0.wireOp",EDGE,"E9"),sQuery(id+"F0.wireOp",EDGE,"E10"),sQuery(id+"F0.wireOp",EDGE,"E16"),sQuery(id+"F0.wireOp",EDGE,"E17"),sQuery(id+"F0.wireOp",EDGE,"E18.trimOffspring"),sQuery(id+"F0.wireOp",EDGE,"E19"),sQuery(id+"F0.wireOp",EDGE,"E20"),subQ2,subQ1,subQ0,subQ6,subQ5,subQ4])],"isStart":true}),makeQuery(id+"F4.opExtrude","CAP_FACE",FACE,{"disambiguationData":[OSD([subQ8,subQ7,subQ6,subQ5,subQ4])],"isStart":true}),makeQuery(id+"F4.opExtrude","CAP_FACE",FACE,{"disambiguationData":[OSD([subQ3,subQ2,subQ1,subQ0])],"isStart":true})]})]});}
            var Q43;
            Q43=makeQuery(id+"F3.opExtrude","CAP_EDGE",EDGE,{"disambiguationData":[OSD([sQuery(id+"F0.wireOp",EDGE,"E18.trimOffspring")])],"isStart":true});
            var Q44;
            Q44=makeQuery(id+"F3.opExtrude","CAP_EDGE",EDGE,{"disambiguationData":[OSD([sQuery(id+"F0.wireOp",EDGE,"E17")])],"isStart":true});
            var Q45;
            Q45=makeQuery(id+"F3.opExtrude","CAP_EDGE",EDGE,{"disambiguationData":[OSD([sQuery(id+"F0.wireOp",EDGE,"E8")])],"isStart":true});
            var Q46;
            Q46=makeQuery(id+"F3.opExtrude","CAP_EDGE",EDGE,{"disambiguationData":[OSD([sQuery(id+"F0.wireOp",EDGE,"E16")])],"isStart":true});
            var Q47;
            Q47=makeQuery(id+"F3.opExtrude","CAP_EDGE",EDGE,{"disambiguationData":[OSD([sQuery(id+"F0.wireOp",EDGE,"E3")])],"isStart":true});
            var Q48;
            {var subQ0=sQuery(id+"F0.wireOp",EDGE,"E31");var subQ1=sQuery(id+"F0.wireOp",EDGE,"E29");var subQ2=sQuery(id+"F0.wireOp",EDGE,"E21.trimOffspring");var subQ3=sQuery(id+"F0.wireOp",EDGE,"E2");var subQ4=sQuery(id+"F0.wireOp",EDGE,"E34");var subQ5=sQuery(id+"F0.wireOp",EDGE,"E33.MirrorCS");var subQ6=sQuery(id+"F0.wireOp",EDGE,"E32.MirrorC");var subQ7=sQuery(id+"F0.wireOp",EDGE,"E1");var subQ8=sQuery(id+"F0.wireOp",EDGE,"E0");var subQ9=sQuery(id+"F0.wireOp",EDGE,"E3");Q48=makeQuery(id+"F10.opChamfer","BLEND_EDGE",EDGE,{"blendedFrom":[makeQuery(id+"F8.boolean.opBoolean","MERGE",EDGE,{"derivedFrom":[makeQuery(id+"F3.opExtrude","SWEPT_EDGE",EDGE,{"disambiguationData":[OSD([subQ3,subQ9])]}),makeQuery(id+"F8.opExtrude","SWEPT_EDGE",EDGE,{"disambiguationData":[OSD([sQuery(id+"F2.wireOp",EDGE,"E38.0.3"),sQuery(id+"F2.wireOp",EDGE,"E38.0.4")])]})]}),makeQuery(id+"F4.boolean.opBoolean","MERGE",FACE,{"derivedFrom":[makeQuery(id+"F3.opExtrude","CAP_FACE",FACE,{"disambiguationData":[OSD([subQ8,subQ7,subQ3,subQ9,sQuery(id+"F0.wireOp",EDGE,"E8"),sQuery(id+"F0.wireOp",EDGE,"E9"),sQuery(id+"F0.wireOp",EDGE,"E10"),sQuery(id+"F0.wireOp",EDGE,"E16"),sQuery(id+"F0.wireOp",EDGE,"E17"),sQuery(id+"F0.wireOp",EDGE,"E18.trimOffspring"),sQuery(id+"F0.wireOp",EDGE,"E19"),sQuery(id+"F0.wireOp",EDGE,"E20"),subQ2,subQ1,subQ0,subQ6,subQ5,subQ4])],"isStart":true}),makeQuery(id+"F4.opExtrude","CAP_FACE",FACE,{"disambiguationData":[OSD([subQ8,subQ7,subQ6,subQ5,subQ4])],"isStart":true}),makeQuery(id+"F4.opExtrude","CAP_FACE",FACE,{"disambiguationData":[OSD([subQ3,subQ2,subQ1,subQ0])],"isStart":true})]})],"blendedInto":[makeQuery(id+"F4.boolean.opBoolean","MERGE",FACE,{"derivedFrom":[makeQuery(id+"F3.opExtrude","CAP_FACE",FACE,{"disambiguationData":[OSD([subQ8,subQ7,subQ3,subQ9,sQuery(id+"F0.wireOp",EDGE,"E8"),sQuery(id+"F0.wireOp",EDGE,"E9"),sQuery(id+"F0.wireOp",EDGE,"E10"),sQuery(id+"F0.wireOp",EDGE,"E16"),sQuery(id+"F0.wireOp",EDGE,"E17"),sQuery(id+"F0.wireOp",EDGE,"E18.trimOffspring"),sQuery(id+"F0.wireOp",EDGE,"E19"),sQuery(id+"F0.wireOp",EDGE,"E20"),subQ2,subQ1,subQ0,subQ6,subQ5,subQ4])],"isStart":true}),makeQuery(id+"F4.opExtrude","CAP_FACE",FACE,{"disambiguationData":[OSD([subQ8,subQ7,subQ6,subQ5,subQ4])],"isStart":true}),makeQuery(id+"F4.opExtrude","CAP_FACE",FACE,{"disambiguationData":[OSD([subQ3,subQ2,subQ1,subQ0])],"isStart":true})]})]});}
            var Q49;
            {var subQ0=sQuery(id+"F0.wireOp",EDGE,"E2");Q49=makeQuery(id+"F4.boolean.opBoolean","MERGE",EDGE,{"derivedFrom":[makeQuery(id+"F3.opExtrude","CAP_EDGE",EDGE,{"disambiguationData":[OSD([subQ0])],"isStart":true}),makeQuery(id+"F4.opExtrude","CAP_EDGE",EDGE,{"disambiguationData":[OSD([subQ0])],"isStart":true})]});}
            fillet(context, id + "F11", {"entities" : qUnion([Q0, Q1, Q2, Q3, Q4, Q5, Q6, Q7, Q8, Q9, Q10, Q11, Q12, Q13, Q14, Q15, Q16, Q17, Q18, Q19, Q20, Q21, Q22, Q23, Q24, Q25, Q26, Q27, Q28, Q29, Q30, Q31, Q32, Q33, Q34, Q35, Q36, Q37, Q38, Q39, Q40, Q41, Q42, Q43, Q44, Q45, Q46, Q47, Q48, Q49]), "radius" : .2 * mm, "tangentPropagation" : true, "allowEdgeOverflow" : false});
        }
    });
